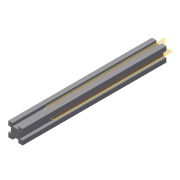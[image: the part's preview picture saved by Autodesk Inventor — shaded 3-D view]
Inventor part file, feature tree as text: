
AUTODESK INVENTOR PART (.ipt)
format: ipt  version: 2019.4 (Build 234330000, 330)  size: 111,616 bytes
history: native  units: mm
features: plane x2, extrude x1, sketch x1
ambient origin geometry x8: Origin, YZ Plane, XZ Plane, XY Plane, X Axis, Y Axis, Z Axis, Center Point
bodies: Solid1 (feature_tree)
feature tree (4):
  extrude  "Extrusion1"  Depth=20.0mm
  plane  "Work Plane1"
  plane  "Work Plane2"
  sketch  "Sketch1"  dims[d0=20.0mm d1=20.0mm d2=8.0mm d3=8.0mm d4=8.0mm d5=8.0mm d6=8.0mm d7=8.0mm d8=8.0mm d9=8.0mm d10=200.0mm d11=0.0mm]
